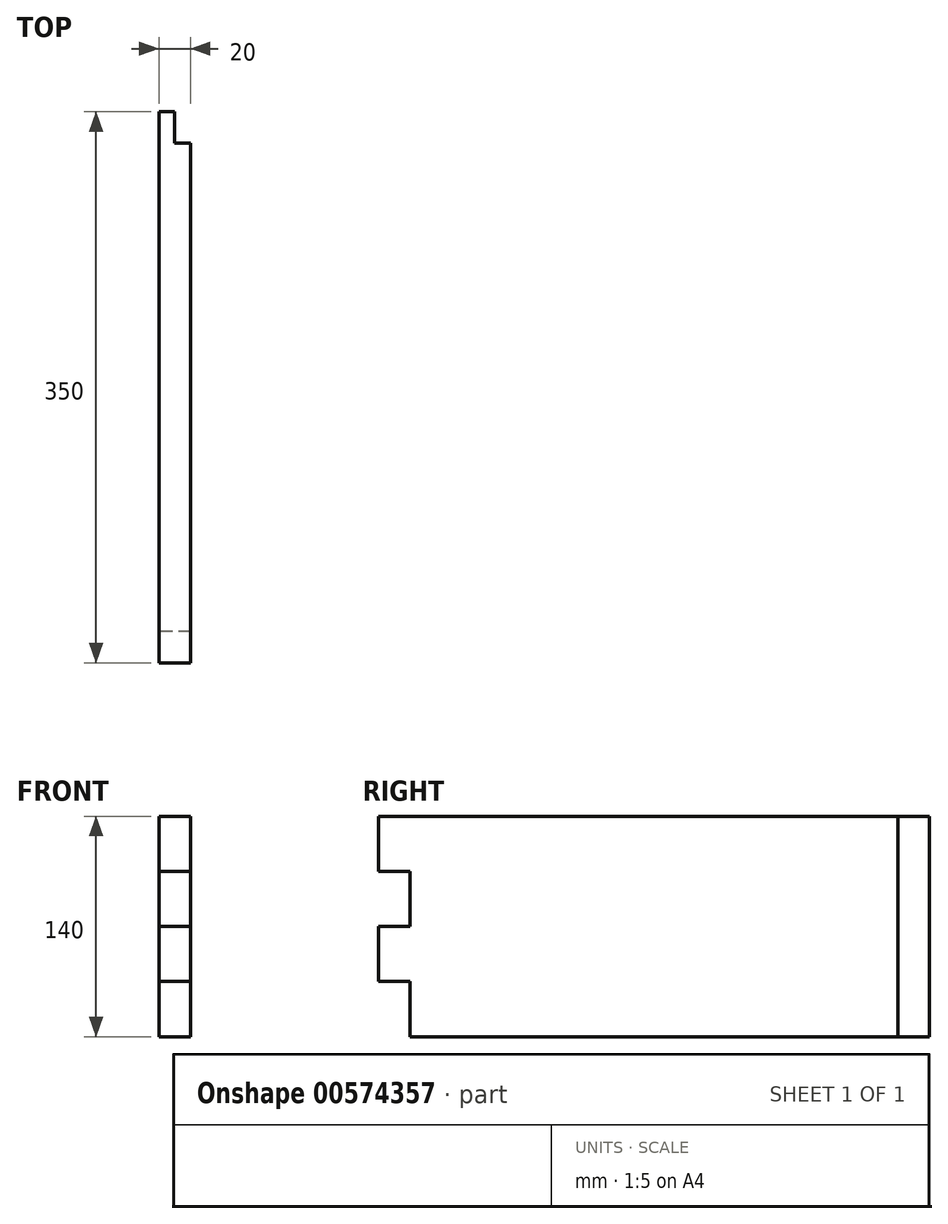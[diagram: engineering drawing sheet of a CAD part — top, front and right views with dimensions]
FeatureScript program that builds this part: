
annotation { "Feature Type Name" : "Feature", "Feature Type Description" : "" }
export const myFeature = defineFeature(function(context is Context, id is Id, definition is map)
    precondition{}
    {
        {
            var Q0;
            Q0=qCreatedBy(makeId("Right.planeOp"),FACE);
            var sketch = newSketch(context, id + "F0", { "sketchPlane" : qUnion([Q0])});
            skLineSegment(sketch, "E0.bottom", {"start": v(-207.8, 87.54) * mm, "end": v(142.2, 87.54) * mm});
            skLineSegment(sketch, "E0.top", {"start": v(-187.8, -52.46) * mm, "end": v(142.2, -52.46) * mm});
            skLineSegment(sketch, "E0.right", {"start": v(142.2, 87.54) * mm, "end": v(142.2, -52.46) * mm});
            skLineSegment(sketch, "E1", {"start": v(-187.8, 87.54) * mm, "end": v(-187.8, -52.46) * mm});
            skLineSegment(sketch, "E2", {"start": v(-207.8, 52.54) * mm, "end": v(-187.8, 52.54) * mm});
            skLineSegment(sketch, "E3", {"start": v(-207.8, -17.46) * mm, "end": v(-187.8, -17.46) * mm});
            skLineSegment(sketch, "E4", {"start": v(-207.8, 17.54) * mm, "end": v(-187.8, 17.54) * mm});
            skLineSegment(sketch, "E5", {"start": v(-207.8, 87.54) * mm, "end": v(-207.8, 52.54) * mm});
            skLineSegment(sketch, "E6", {"start": v(-207.8, 17.54) * mm, "end": v(-207.8, -17.46) * mm});
            skPoint(sketch, "E7.orphan", {"position": v(-207.8, -52.46) * mm});
            skSolve(sketch);
        }
        {
            var Q0;
            Q0 = qSketchRegion(id + "F0", true);
            extrude(context, id + "F1", {"entities" : qUnion([Q0]), "depth" : 20 * mm, "offsetDistance" : 25 * mm});
        }
        {
            var Q0;
            Q0=makeQuery(id+"F1.opExtrude","SWEPT_FACE",FACE,{"disambiguationData":[OSD([sQuery(id+"F0.wireOp",EDGE,"E0.right")])]});
            var sketch = newSketch(context, id + "F2", { "sketchPlane" : qUnion([Q0])});
            skLineSegment(sketch, "E8", {"start": v(-10, 87.54) * mm, "end": v(-10, -52.46) * mm});
            skSolve(sketch);
        }
        {
            var Q0;
            {var subQ0=sQuery(id+"F2.wireOp",EDGE,"E8");Q0=makeQuery(id+"F2.imprint","IMPRINT",FACE,{"disambiguationData":[TD([[makeQuery(id+"F2.imprint","IMPRINT",EDGE,{"derivedFrom":subQ0}),-1.0]])]});}
            extrude(context, id + "F3", {"entities" : qUnion([Q0]), "operationType" : NewBodyOperationType.REMOVE, "oppositeDirection" : true, "depth" : 20 * mm, "offsetDistance" : 25 * mm});
        }
    });
